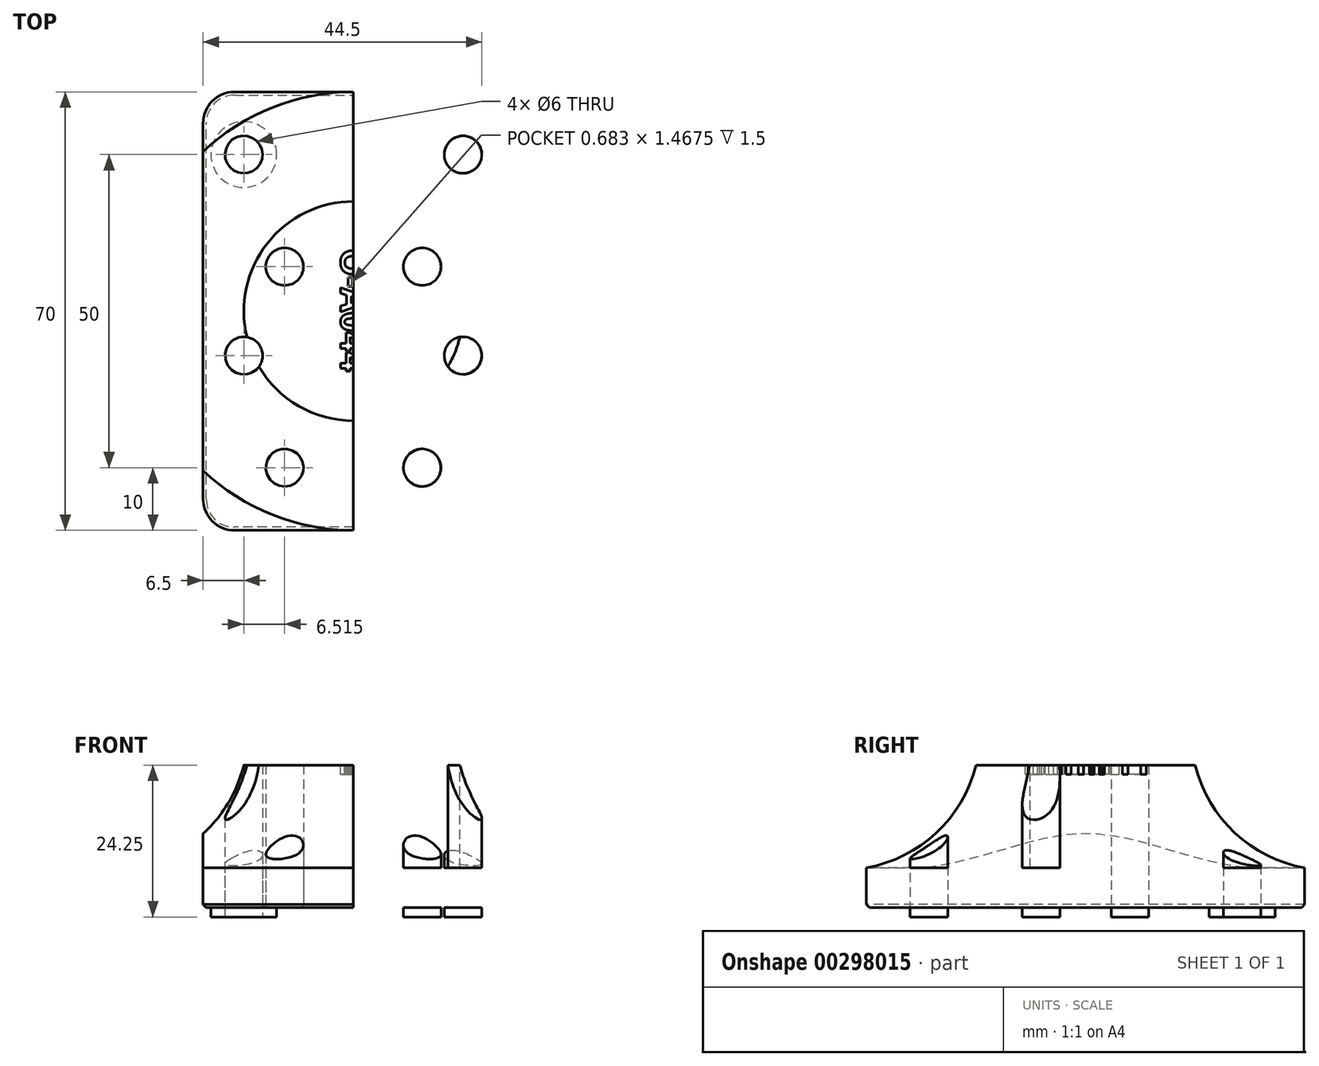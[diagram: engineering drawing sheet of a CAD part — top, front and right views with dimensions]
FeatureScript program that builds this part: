
annotation { "Feature Type Name" : "Feature", "Feature Type Description" : "" }
export const myFeature = defineFeature(function(context is Context, id is Id, definition is map)
    precondition{}
    {
        {
            var Q0;
            Q0=qCreatedBy(makeId("Top.planeOp"),FACE);
            var sketch = newSketch(context, id + "F0", { "sketchPlane" : qUnion([Q0])});
            skLineSegment(sketch, "E0.bottom", {"start": v(-24, 35) * mm, "end": v(24, 35) * mm});
            skLineSegment(sketch, "E0.top", {"start": v(-24, -35) * mm, "end": v(24, -35) * mm});
            skLineSegment(sketch, "E0.left", {"start": v(-24, 35) * mm, "end": v(-24, -35) * mm});
            skLineSegment(sketch, "E0.right", {"start": v(24, 35) * mm, "end": v(24, -35) * mm});
            skPoint(sketch, "E0.middle", {"position": v(0, 0) * mm});
            skCircle(sketch, "E1", {"center": v(-10.98, 7.1) * mm, "radius": 3 * mm});
            skCircle(sketch, "E2", {"center": v(-17.5, 25) * mm, "radius": 3 * mm});
            skLineSegment(sketch, "E3", {"start": v(-17.5, 25) * mm, "end": v(-10.98, 7.1) * mm, "construction": true});
            skCircle(sketch, "E4", {"center": v(-10.98, -25) * mm, "radius": 3 * mm});
            skCircle(sketch, "E5", {"center": v(-17.5, -7.1) * mm, "radius": 3 * mm});
            skLineSegment(sketch, "E6", {"start": v(-17.5, -7.1) * mm, "end": v(0, -7.1) * mm, "construction": true});
            skLineSegment(sketch, "E7", {"start": v(-17.5, -7.1) * mm, "end": v(-10.98, -25) * mm, "construction": true});
            skLineSegment(sketch, "E8", {"start": v(-17.5, 25) * mm, "end": v(-24, 25) * mm, "construction": true});
            skCircle(sketch, "E9.MirrorC", {"center": v(17.5, 25) * mm, "radius": 3 * mm});
            skCircle(sketch, "E10.MirrorC", {"center": v(10.98, 7.1) * mm, "radius": 3 * mm});
            skCircle(sketch, "E11.MirrorC", {"center": v(17.5, -7.1) * mm, "radius": 3 * mm});
            skCircle(sketch, "E12.MirrorC", {"center": v(10.98, -25) * mm, "radius": 3 * mm});
            skLineSegment(sketch, "E13", {"start": v(0, 35) * mm, "end": v(0, -35) * mm});
            skSolve(sketch);
        }
        {
            var Q0;
            {var subQ0=sQuery(id+"F0.wireOp",EDGE,"E0.left");Q0=makeQuery(id+"F0.imprint","IMPRINT",FACE,{"disambiguationData":[TD([[makeQuery(id+"F0.imprint","IMPRINT",EDGE,{"derivedFrom":subQ0}),1.0]])]});}
            extrude(context, id + "F1", {"entities" : qUnion([Q0]), "depth" : 22.75 * mm});
        }
        {
            var Q0;
            Q0=makeQuery(id+"F1.opExtrude","SWEPT_EDGE",EDGE,{"disambiguationData":[OSD([sQuery(id+"F0.wireOp",EDGE,"E0.top"),sQuery(id+"F0.wireOp",EDGE,"E0.left")])]});
            var Q1;
            Q1=makeQuery(id+"F1.opExtrude","SWEPT_EDGE",EDGE,{"disambiguationData":[OSD([sQuery(id+"F0.wireOp",EDGE,"E0.bottom"),sQuery(id+"F0.wireOp",EDGE,"E0.left")])]});
            fillet(context, id + "F2", {"entities" : qUnion([Q0, Q1]), "radius" : 5 * mm, "tangentPropagation" : true, "allowEdgeOverflow" : false});
        }
        {
            var Q0;
            Q0=makeQuery(id+"F1.opExtrude","CAP_EDGE",EDGE,{"disambiguationData":[OSD([sQuery(id+"F0.wireOp",EDGE,"E0.bottom")])],"isStart":true});
            var Q1;
            Q1=makeQuery(id+"F1.opExtrude","CAP_EDGE",EDGE,{"disambiguationData":[OSD([sQuery(id+"F0.wireOp",EDGE,"E0.left")])],"isStart":true});
            var Q2;
            Q2=makeQuery(id+"F1.opExtrude","CAP_EDGE",EDGE,{"disambiguationData":[OSD([sQuery(id+"F0.wireOp",EDGE,"E0.top")])],"isStart":true});
            chamfer(context, id + "F3", {"entities" : qUnion([Q0, Q1, Q2]), "width" : 0.5 * mm, "tangentPropagation" : true});
        }
        {
            var Q0;
            Q0=makeQuery(id+"F1.opExtrude","CAP_FACE",FACE,{"disambiguationData":[OSD([sQuery(id+"F0.wireOp",EDGE,"E0.bottom"),sQuery(id+"F0.wireOp",EDGE,"E0.top"),sQuery(id+"F0.wireOp",EDGE,"E0.left"),sQuery(id+"F0.wireOp",EDGE,"E0.right"),sQuery(id+"F0.wireOp",EDGE,"E1"),sQuery(id+"F0.wireOp",EDGE,"E2"),sQuery(id+"F0.wireOp",EDGE,"E4"),sQuery(id+"F0.wireOp",EDGE,"E5"),sQuery(id+"F0.wireOp",EDGE,"E9.MirrorC"),sQuery(id+"F0.wireOp",EDGE,"E10.MirrorC"),sQuery(id+"F0.wireOp",EDGE,"E11.MirrorC"),sQuery(id+"F0.wireOp",EDGE,"E12.MirrorC")])],"isStart":false});
            var sketch = newSketch(context, id + "F4", { "sketchPlane" : qUnion([Q0])});
            skSolve(sketch);
        }
        {
            var Q0;
            {var subQ3=sQuery(id+"F0.wireOp",EDGE,"E1");Q0=makeQuery(id+"F4.imprint","IMPRINT",FACE,{"disambiguationData":[TD([[makeQuery(id+"F4.imprint","IMPRINT",EDGE,{"derivedFrom":makeQuery(id+"F1.opExtrude","CAP_EDGE",EDGE,{"disambiguationData":[OSD([subQ3])],"isStart":false})}),-1.0]])]});}
            var sketch = newSketch(context, id + "F5", { "sketchPlane" : qUnion([Q0])});
            skArc(sketch, "E14", {"start": v(0, 17.5) * mm, "mid": v(-17.5, 0) * mm, "end": v(0, -17.5) * mm});
            skSolve(sketch);
        }
        {
            var Q0;
            {var subQ8=sQuery(id+"F0.wireOp",EDGE,"E2");Q0=makeQuery(id+"F5.imprint","IMPRINT",FACE,{"disambiguationData":[TD([[makeQuery(id+"F5.imprint","IMPRINT",EDGE,{"derivedFrom":makeQuery(id+"F4.imprint","IMPRINT",EDGE,{"derivedFrom":makeQuery(id+"F1.opExtrude","CAP_EDGE",EDGE,{"disambiguationData":[OSD([subQ8])],"isStart":false})})}),-1.0]])]});}
            extrude(context, id + "F6", {"entities" : qUnion([Q0]), "operationType" : NewBodyOperationType.REMOVE, "oppositeDirection" : true, "depth" : 16.4 * mm});
        }
        {
            var Q0;
            Q0=makeQuery(id+"F1.opExtrude","SWEPT_BODY",BODY,{"disambiguationData":[OSD([sQuery(id+"F0.wireOp",EDGE,"E0.bottom"),sQuery(id+"F0.wireOp",EDGE,"E0.top"),sQuery(id+"F0.wireOp",EDGE,"E0.left"),sQuery(id+"F0.wireOp",EDGE,"E1"),sQuery(id+"F0.wireOp",EDGE,"E2"),sQuery(id+"F0.wireOp",EDGE,"E4"),sQuery(id+"F0.wireOp",EDGE,"E5"),sQuery(id+"F0.wireOp",EDGE,"E13")])]});
            var Q1;
            Q1=qCreatedBy(makeId("Right.planeOp"),FACE);
            mirror(context, id + "F7", {"operationType" : NewBodyOperationType.ADD, "entities" : qUnion([Q0]), "mirrorPlane" : qUnion([Q1])});
        }
        {
            var Q0;
            {var subQ0=makeQuery(id+"F1.opExtrude","CAP_FACE",FACE,{"disambiguationData":[OSD([sQuery(id+"F0.wireOp",EDGE,"E0.bottom"),sQuery(id+"F0.wireOp",EDGE,"E0.top"),sQuery(id+"F0.wireOp",EDGE,"E0.left"),sQuery(id+"F0.wireOp",EDGE,"E1"),sQuery(id+"F0.wireOp",EDGE,"E2"),sQuery(id+"F0.wireOp",EDGE,"E4"),sQuery(id+"F0.wireOp",EDGE,"E5"),sQuery(id+"F0.wireOp",EDGE,"E13")])],"isStart":false});Q0=makeQuery(id+"Ftgeyd71CWDRaZ8_1.boolean.opBoolean","MERGE",FACE,{"derivedFrom":[subQ0,makeQuery(id+"Ftgeyd71CWDRaZ8_1.opPattern","COPY",FACE,{"derivedFrom":subQ0,"instanceName":"1"})]});}
            var sketch = newSketch(context, id + "F8", { "sketchPlane" : qUnion([Q0])});
            skText(sketch, "E15", { "text": "O-A044", "fontName": "OpenSans-Bold.ttf"});
            skPoint(sketch, "E16", {"position": v(0, 0) * mm});
            const initialGuessF8  = {"E15": [-0.00202, 0.01, 0, -1, 0.00403]};
            skSetInitialGuess(sketch, initialGuessF8);
            skSolve(sketch);
        }
        {
            var Q0;
            Q0=qSketchRegion(id+"F8",true);
            extrude(context, id + "F9", {"entities" : qUnion([Q0]), "operationType" : NewBodyOperationType.REMOVE, "oppositeDirection" : true, "depth" : 1.5 * mm});
        }
        {
            var Q0;
            Q0=qCreatedBy(makeId("Right.planeOp"),FACE);
            var sketch = newSketch(context, id + "F10", { "sketchPlane" : qUnion([Q0])});
            skArc(sketch, "E17", {"start": v(17.5, 22.75) * mm, "mid": v(23.82, 11.96) * mm, "end": v(35, 6.35) * mm});
            skLineSegment(sketch, "E18", {"start": v(17.5, 22.75) * mm, "end": v(17.5, 6.35) * mm});
            skLineSegment(sketch, "E19", {"start": v(17.5, 6.35) * mm, "end": v(35, 6.35) * mm});
            skSolve(sketch);
        }
        {
            var Q0;
            Q0=qCreatedBy(makeId("Front.planeOp"),FACE);
            var sketch = newSketch(context, id + "F11", { "sketchPlane" : qUnion([Q0])});
            skLineSegment(sketch, "E20", {"start": v(0, -27.65) * mm, "end": v(0, 47.18) * mm, "construction": true});
            skSolve(sketch);
        }
        {
            var Q0;
            Q0=makeQuery(id+"F10.imprint","IMPRINT",FACE,{"disambiguationData":[TD([[makeQuery(id+"F10.imprint","IMPRINT",EDGE,{"derivedFrom":sQuery(id+"F10.wireOp",EDGE,"E17")}),-1.0]])]});
            var Q1;
            Q1=sQuery(id+"F11.wireOp",EDGE,"E20");
            revolve(context, id + "F12", {"operationType" : NewBodyOperationType.ADD, "entities" : qUnion([Q0]), "axis" : qUnion([Q1]), "revolveType" : RevolveType.FULL});
        }
        {
            var Q0;
            {var subQ0=sQuery(id+"F0.wireOp",EDGE,"E0.left");Q0=makeQuery(id+"F12.boolean.opBoolean","SPLIT",FACE,{"disambiguationData":[TD([makeQuery(id+"F1.opExtrude","SWEPT_FACE",FACE,{"disambiguationData":[OSD([subQ0])]})])],"derivedFrom":makeQuery(id+"F12.opRevolve","SWEPT_FACE",FACE,{"disambiguationData":[OSD([sQuery(id+"F10.wireOp",EDGE,"E19")])]})});}
            var Q1;
            {var subQ0=sQuery(id+"F0.wireOp",EDGE,"E0.left");Q1=makeQuery(id+"F12.boolean.opBoolean","SPLIT",FACE,{"disambiguationData":[TD([makeQuery(id+"F7.opPattern","COPY",FACE,{"derivedFrom":makeQuery(id+"F1.opExtrude","SWEPT_FACE",FACE,{"disambiguationData":[OSD([subQ0])]}),"instanceName":"1"})])],"derivedFrom":makeQuery(id+"F12.opRevolve","SWEPT_FACE",FACE,{"disambiguationData":[OSD([sQuery(id+"F10.wireOp",EDGE,"E19")])]})});}
            extrude(context, id + "F13", {"entities" : qUnion([Q0, Q1]), "operationType" : NewBodyOperationType.REMOVE, "endBound" : BoundingType.THROUGH_ALL, "oppositeDirection" : true, "depth" : 25 * mm});
        }
        {
            var Q0;
            Q0=makeQuery(id+"F0.imprint","IMPRINT",FACE,{"disambiguationData":[TD([[makeQuery(id+"F0.imprint","IMPRINT",EDGE,{"derivedFrom":sQuery(id+"F0.wireOp",EDGE,"E5")}),1.0]])]});
            var Q1;
            Q1=makeQuery(id+"F0.imprint","IMPRINT",FACE,{"disambiguationData":[TD([[makeQuery(id+"F0.imprint","IMPRINT",EDGE,{"derivedFrom":sQuery(id+"F0.wireOp",EDGE,"E4")}),1.0]])]});
            var Q2;
            Q2=makeQuery(id+"F0.imprint","IMPRINT",FACE,{"disambiguationData":[TD([[makeQuery(id+"F0.imprint","IMPRINT",EDGE,{"derivedFrom":sQuery(id+"F0.wireOp",EDGE,"E1")}),1.0]])]});
            var Q3;
            Q3=makeQuery(id+"F0.imprint","IMPRINT",FACE,{"disambiguationData":[TD([[makeQuery(id+"F0.imprint","IMPRINT",EDGE,{"derivedFrom":sQuery(id+"F0.wireOp",EDGE,"E2")}),1.0]])]});
            var Q4;
            Q4=makeQuery(id+"F0.imprint","IMPRINT",FACE,{"disambiguationData":[TD([[makeQuery(id+"F0.imprint","IMPRINT",EDGE,{"derivedFrom":sQuery(id+"F0.wireOp",EDGE,"E10.MirrorC")}),-1.0]])]});
            var Q5;
            Q5=makeQuery(id+"F0.imprint","IMPRINT",FACE,{"disambiguationData":[TD([[makeQuery(id+"F0.imprint","IMPRINT",EDGE,{"derivedFrom":sQuery(id+"F0.wireOp",EDGE,"E11.MirrorC")}),-1.0]])]});
            var Q6;
            Q6=makeQuery(id+"F0.imprint","IMPRINT",FACE,{"disambiguationData":[TD([[makeQuery(id+"F0.imprint","IMPRINT",EDGE,{"derivedFrom":sQuery(id+"F0.wireOp",EDGE,"E12.MirrorC")}),-1.0]])]});
            var Q7;
            Q7=makeQuery(id+"F0.imprint","IMPRINT",FACE,{"disambiguationData":[TD([[makeQuery(id+"F0.imprint","IMPRINT",EDGE,{"derivedFrom":sQuery(id+"F0.wireOp",EDGE,"E9.MirrorC")}),-1.0]])]});
            extrude(context, id + "F14", {"entities" : qUnion([Q0, Q1, Q2, Q3, Q4, Q5, Q6, Q7]), "operationType" : NewBodyOperationType.REMOVE, "endBound" : BoundingType.THROUGH_ALL, "depth" : 25 * mm});
        }
        {
            var Q0;
            {var subQ0=sQuery(id+"F0.wireOp",EDGE,"E0.right");Q0=makeQuery(id+"F0.imprint","IMPRINT",FACE,{"disambiguationData":[TD([[makeQuery(id+"F0.imprint","IMPRINT",EDGE,{"derivedFrom":subQ0}),-1.0]])]});}
            var sketch = newSketch(context, id + "F15", { "sketchPlane" : qUnion([Q0])});
            skCircle(sketch, "E21.0", {"center": v(17.5, 25) * mm, "radius": 3 * mm});
            skCircle(sketch, "E22.0", {"center": v(10.98, 7.1) * mm, "radius": 3 * mm});
            skCircle(sketch, "E23.0", {"center": v(17.5, -7.1) * mm, "radius": 3 * mm});
            skCircle(sketch, "E24.0", {"center": v(10.98, -25) * mm, "radius": 3 * mm});
            skCircle(sketch, "E25", {"center": v(17.5, 25) * mm, "radius": 5.25 * mm});
            skCircle(sketch, "E26", {"center": v(10.98, 7.1) * mm, "radius": 5.25 * mm});
            skCircle(sketch, "E27", {"center": v(17.5, -7.1) * mm, "radius": 5.25 * mm});
            skCircle(sketch, "E28", {"center": v(10.98, -25) * mm, "radius": 5.25 * mm});
            skCircle(sketch, "E29.MirrorC", {"center": v(-17.5, 25) * mm, "radius": 3 * mm});
            skCircle(sketch, "E30.MirrorC", {"center": v(-17.5, 25) * mm, "radius": 5.25 * mm});
            skCircle(sketch, "E31.MirrorC", {"center": v(-10.98, 7.1) * mm, "radius": 5.25 * mm});
            skCircle(sketch, "E32.MirrorC", {"center": v(-10.98, 7.1) * mm, "radius": 3 * mm});
            skCircle(sketch, "E33.MirrorC", {"center": v(-17.5, -7.1) * mm, "radius": 5.25 * mm});
            skCircle(sketch, "E34.MirrorC", {"center": v(-17.5, -7.1) * mm, "radius": 3 * mm});
            skCircle(sketch, "E35.MirrorC", {"center": v(-10.98, -25) * mm, "radius": 5.25 * mm});
            skCircle(sketch, "E36.MirrorC", {"center": v(-10.98, -25) * mm, "radius": 3 * mm});
            skSolve(sketch);
        }
        {
            var Q0;
            Q0=makeQuery(id+"F15.imprint","IMPRINT",FACE,{"disambiguationData":[TD([[makeQuery(id+"F15.imprint","IMPRINT",EDGE,{"derivedFrom":sQuery(id+"F15.wireOp",EDGE,"E21.0")}),1.0]])]});
            var Q1;
            Q1=makeQuery(id+"F15.imprint","IMPRINT",FACE,{"disambiguationData":[TD([[makeQuery(id+"F15.imprint","IMPRINT",EDGE,{"derivedFrom":sQuery(id+"F15.wireOp",EDGE,"E22.0")}),1.0]])]});
            var Q2;
            Q2=makeQuery(id+"F15.imprint","IMPRINT",FACE,{"disambiguationData":[TD([[makeQuery(id+"F15.imprint","IMPRINT",EDGE,{"derivedFrom":sQuery(id+"F15.wireOp",EDGE,"E23.0")}),1.0]])]});
            var Q3;
            Q3=makeQuery(id+"F15.imprint","IMPRINT",FACE,{"disambiguationData":[TD([[makeQuery(id+"F15.imprint","IMPRINT",EDGE,{"derivedFrom":sQuery(id+"F15.wireOp",EDGE,"E24.0")}),1.0]])]});
            var Q4;
            Q4=makeQuery(id+"F15.imprint","IMPRINT",FACE,{"disambiguationData":[TD([[makeQuery(id+"F15.imprint","IMPRINT",EDGE,{"derivedFrom":sQuery(id+"F15.wireOp",EDGE,"E35.MirrorC")}),-1.0]])]});
            var Q5;
            Q5=makeQuery(id+"F15.imprint","IMPRINT",FACE,{"disambiguationData":[TD([[makeQuery(id+"F15.imprint","IMPRINT",EDGE,{"derivedFrom":sQuery(id+"F15.wireOp",EDGE,"E33.MirrorC")}),-1.0]])]});
            var Q6;
            Q6=makeQuery(id+"F15.imprint","IMPRINT",FACE,{"disambiguationData":[TD([[makeQuery(id+"F15.imprint","IMPRINT",EDGE,{"derivedFrom":sQuery(id+"F15.wireOp",EDGE,"E31.MirrorC")}),-1.0]])]});
            var Q7;
            Q7=makeQuery(id+"F15.imprint","IMPRINT",FACE,{"disambiguationData":[TD([[makeQuery(id+"F15.imprint","IMPRINT",EDGE,{"derivedFrom":sQuery(id+"F15.wireOp",EDGE,"E29.MirrorC")}),-1.0]])]});
            extrude(context, id + "F16", {"entities" : qUnion([Q0, Q1, Q2, Q3, Q4, Q5, Q6, Q7]), "operationType" : NewBodyOperationType.ADD, "oppositeDirection" : true, "depth" : 1.5 * mm});
        }
    });
